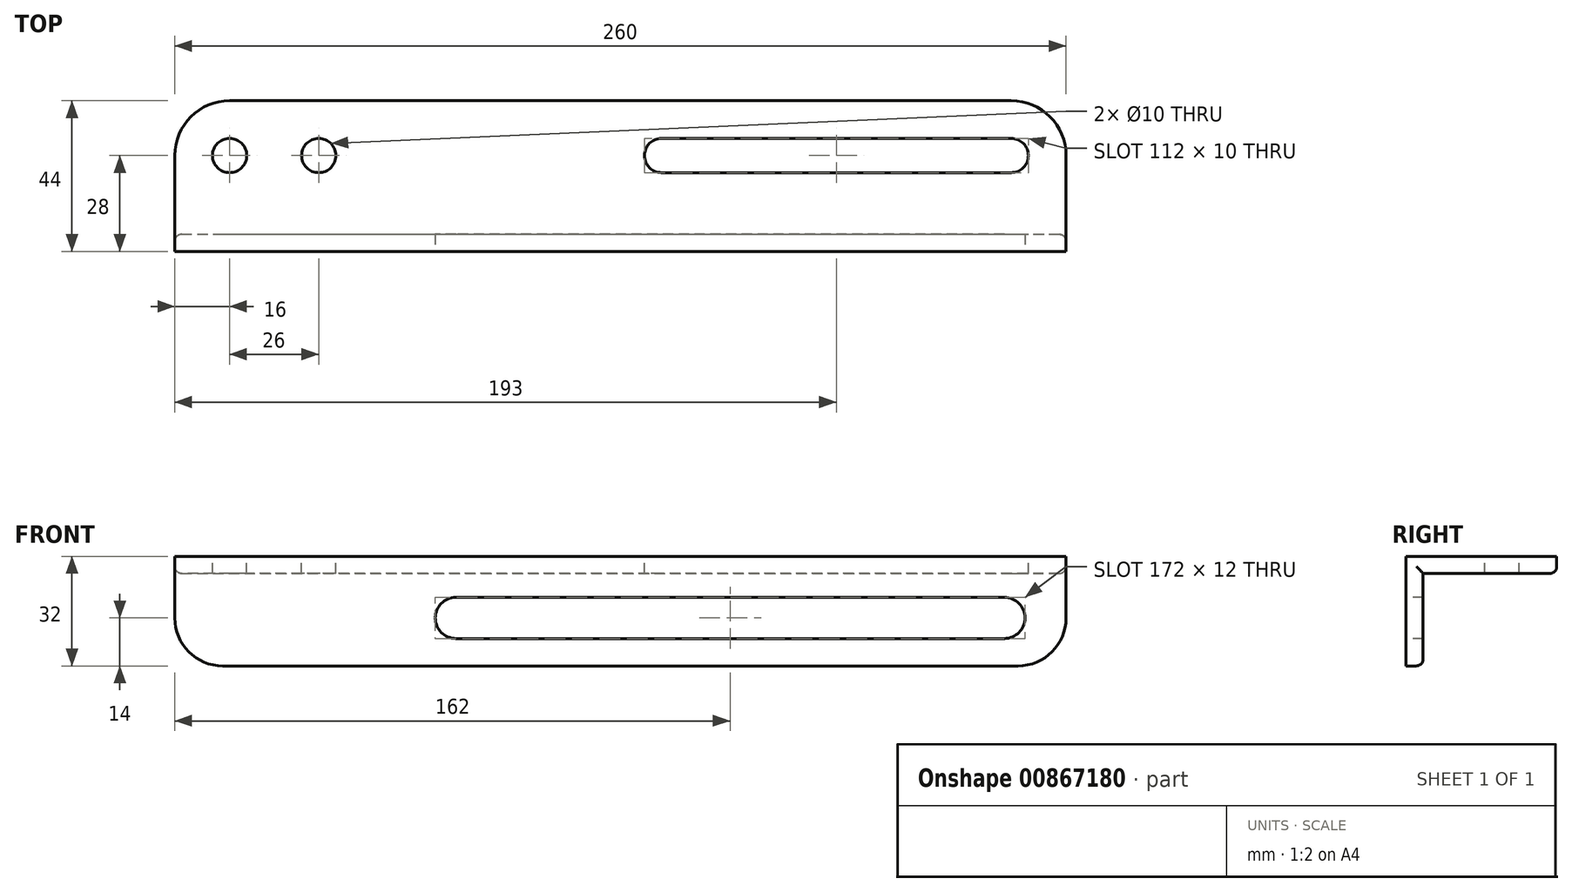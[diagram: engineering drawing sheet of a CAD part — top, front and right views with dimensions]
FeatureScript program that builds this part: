
annotation { "Feature Type Name" : "Feature", "Feature Type Description" : "" }
export const myFeature = defineFeature(function(context is Context, id is Id, definition is map)
    precondition{}
    {
        {
            var Q0;
            Q0=qCreatedBy(makeId("Top.planeOp"),FACE);
            var sketch = newSketch(context, id + "F0", { "sketchPlane" : qUnion([Q0])});
            skLineSegment(sketch, "E0", {"start": v(130, 0) * mm, "end": v(-130, 0) * mm});
            skLineSegment(sketch, "E1", {"start": v(130, 0) * mm, "end": v(130, 28) * mm});
            skLineSegment(sketch, "E2", {"start": v(114, 44) * mm, "end": v(-114, 44) * mm});
            skLineSegment(sketch, "E3", {"start": v(-130, 28) * mm, "end": v(-130, 0) * mm});
            skPoint(sketch, "E4.visualSharp", {"position": v(130, 44) * mm});
            skArc(sketch, "E4.filletArc", {"start": v(130, 28) * mm, "mid": v(125.31, 39.31) * mm, "end": v(114, 44) * mm});
            skPoint(sketch, "E5.visualSharp", {"position": v(-130, 44) * mm});
            skArc(sketch, "E5.filletArc", {"start": v(-114, 44) * mm, "mid": v(-125.31, 39.31) * mm, "end": v(-130, 28) * mm});
            skSolve(sketch);
        }
        {
            var Q0;
            Q0=makeQuery(id+"F0.imprint","IMPRINT",FACE,{"disambiguationData":[TD([[makeQuery(id+"F0.imprint","IMPRINT",EDGE,{"derivedFrom":sQuery(id+"F0.wireOp",EDGE,"E0")}),-1.0]])]});
            extrude(context, id + "F1", {"entities" : qUnion([Q0]), "oppositeDirection" : true, "depth" : 5 * mm, "offsetDistance" : 25 * mm});
        }
        {
            var Q0;
            Q0=makeQuery(id+"F1.opExtrude","CAP_FACE",FACE,{"disambiguationData":[OSD([sQuery(id+"F0.wireOp",EDGE,"E0"),sQuery(id+"F0.wireOp",EDGE,"E1"),sQuery(id+"F0.wireOp",EDGE,"E2"),sQuery(id+"F0.wireOp",EDGE,"E3"),sQuery(id+"F0.wireOp",EDGE,"E4.filletArc"),sQuery(id+"F0.wireOp",EDGE,"E5.filletArc")])],"isStart":true});
            var sketch = newSketch(context, id + "F2", { "sketchPlane" : qUnion([Q0])});
            skLineSegment(sketch, "E6", {"start": v(-149.8, 28) * mm, "end": v(123.32, 28) * mm, "construction": true});
            skLineSegment(sketch, "E7", {"start": v(-114, 41.85) * mm, "end": v(-114, -2.88) * mm, "construction": true});
            skLineSegment(sketch, "E8", {"start": v(-88, 42.48) * mm, "end": v(-88, -4.78) * mm, "construction": true});
            skCircle(sketch, "E9", {"center": v(-114, 28) * mm, "radius": 5 * mm});
            skCircle(sketch, "E10", {"center": v(-88, 28) * mm, "radius": 5 * mm});
            skLineSegment(sketch, "E11", {"start": v(12, 13.35) * mm, "end": v(12, 37.98) * mm, "construction": true});
            skLineSegment(sketch, "E12", {"start": v(114, 14.97) * mm, "end": v(114, 36.5) * mm, "construction": true});
            skLineSegment(sketch, "E13", {"start": v(114, 23) * mm, "end": v(12, 23) * mm});
            skLineSegment(sketch, "E14.MirrorCS", {"start": v(114, 33) * mm, "end": v(12, 33) * mm});
            skArc(sketch, "E15", {"start": v(12, 23) * mm, "mid": v(7, 28) * mm, "end": v(12, 33) * mm});
            skArc(sketch, "E16", {"start": v(114, 33) * mm, "mid": v(119, 28) * mm, "end": v(114, 23) * mm});
            skSolve(sketch);
        }
        {
            var Q0;
            Q0=makeQuery(id+"F2.imprint","IMPRINT",FACE,{"disambiguationData":[TD([[makeQuery(id+"F2.imprint","IMPRINT",EDGE,{"derivedFrom":sQuery(id+"F2.wireOp",EDGE,"E13")}),-1.0]])]});
            var Q1;
            Q1=makeQuery(id+"F2.imprint","IMPRINT",FACE,{"disambiguationData":[TD([[makeQuery(id+"F2.imprint","IMPRINT",EDGE,{"derivedFrom":sQuery(id+"F2.wireOp",EDGE,"E10")}),1.0]])]});
            var Q2;
            Q2=makeQuery(id+"F2.imprint","IMPRINT",FACE,{"disambiguationData":[TD([[makeQuery(id+"F2.imprint","IMPRINT",EDGE,{"derivedFrom":sQuery(id+"F2.wireOp",EDGE,"E9")}),1.0]])]});
            extrude(context, id + "F3", {"entities" : qUnion([Q0, Q1, Q2]), "operationType" : NewBodyOperationType.REMOVE, "oppositeDirection" : true, "depth" : 5 * mm, "offsetDistance" : 25 * mm});
        }
        {
            var Q0;
            Q0=makeQuery(id+"F1.opExtrude","CAP_FACE",FACE,{"disambiguationData":[OSD([sQuery(id+"F0.wireOp",EDGE,"E0"),sQuery(id+"F0.wireOp",EDGE,"E1"),sQuery(id+"F0.wireOp",EDGE,"E2"),sQuery(id+"F0.wireOp",EDGE,"E3"),sQuery(id+"F0.wireOp",EDGE,"E4.filletArc"),sQuery(id+"F0.wireOp",EDGE,"E5.filletArc")])],"isStart":false});
            var sketch = newSketch(context, id + "F4", { "sketchPlane" : qUnion([Q0])});
            skLineSegment(sketch, "E17", {"start": v(130, 0) * mm, "end": v(-130, 0) * mm});
            skLineSegment(sketch, "E18", {"start": v(-130, 0) * mm, "end": v(-130, -5) * mm});
            skLineSegment(sketch, "E19", {"start": v(-130, -5) * mm, "end": v(130, -5) * mm});
            skLineSegment(sketch, "E20", {"start": v(130, -5) * mm, "end": v(130, 0) * mm});
            skSolve(sketch);
        }
        {
            var Q0;
            Q0=makeQuery(id+"F4.imprint","IMPRINT",FACE,{"disambiguationData":[TD([[makeQuery(id+"F4.imprint","IMPRINT",EDGE,{"derivedFrom":sQuery(id+"F4.wireOp",EDGE,"E17")}),1.0]])]});
            extrude(context, id + "F5", {"entities" : qUnion([Q0]), "operationType" : NewBodyOperationType.ADD, "depth" : 27 * mm, "offsetDistance" : 25 * mm});
        }
        {
            var Q0;
            Q0=makeQuery(id+"F5.opExtrude","CAP_EDGE",EDGE,{"disambiguationData":[OSD([sQuery(id+"F4.wireOp",EDGE,"E20")])],"isStart":false});
            var Q1;
            Q1=makeQuery(id+"F5.opExtrude","CAP_EDGE",EDGE,{"disambiguationData":[OSD([sQuery(id+"F4.wireOp",EDGE,"E18")])],"isStart":false});
            fillet(context, id + "F6", {"entities" : qUnion([Q0, Q1]), "radius" : 14 * mm, "tangentPropagation" : true, "allowEdgeOverflow" : false});
        }
        {
            var Q0;
            Q0=makeQuery(id+"F5.boolean.opBoolean","MERGE",FACE,{"derivedFrom":[makeQuery(id+"F1.opExtrude","SWEPT_FACE",FACE,{"disambiguationData":[OSD([sQuery(id+"F0.wireOp",EDGE,"E0")])]}),makeQuery(id+"F5.opExtrude","SWEPT_FACE",FACE,{"disambiguationData":[OSD([sQuery(id+"F4.wireOp",EDGE,"E17")])]})]});
            var sketch = newSketch(context, id + "F7", { "sketchPlane" : qUnion([Q0])});
            skLineSegment(sketch, "E21", {"start": v(183.96, -18) * mm, "end": v(-135.14, -18) * mm, "construction": true});
            skLineSegment(sketch, "E22", {"start": v(112, 13.92) * mm, "end": v(112, -46.51) * mm, "construction": true});
            skLineSegment(sketch, "E23", {"start": v(-48, 7.81) * mm, "end": v(-48, -45.47) * mm, "construction": true});
            skLineSegment(sketch, "E24", {"start": v(112, -12) * mm, "end": v(-48, -12) * mm});
            skLineSegment(sketch, "E25.MirrorCS", {"start": v(112, -24) * mm, "end": v(-48, -24) * mm});
            skArc(sketch, "E26", {"start": v(-48, -24) * mm, "mid": v(-54, -18) * mm, "end": v(-48, -12) * mm});
            skArc(sketch, "E27", {"start": v(112, -12) * mm, "mid": v(118, -18) * mm, "end": v(112, -24) * mm});
            skSolve(sketch);
        }
        {
            var Q0;
            Q0 = qSketchRegion(id + "F7", true);
            extrude(context, id + "F8", {"entities" : qUnion([Q0]), "operationType" : NewBodyOperationType.REMOVE, "oppositeDirection" : true, "depth" : 5 * mm, "offsetDistance" : 25 * mm});
        }
        {
            var Q0;
            Q0=makeQuery(id+"F5.opExtrude","CAP_EDGE",EDGE,{"disambiguationData":[OSD([sQuery(id+"F4.wireOp",EDGE,"E19")])],"isStart":false});
            var Q1;
            Q1=makeQuery(id+"F1.opExtrude","CAP_EDGE",EDGE,{"disambiguationData":[OSD([sQuery(id+"F0.wireOp",EDGE,"E2")])],"isStart":false});
            var Q2;
            Q2=makeQuery(id+"F5.opExtrude","CAP_EDGE",EDGE,{"disambiguationData":[OSD([sQuery(id+"F4.wireOp",EDGE,"E19")])],"isStart":true});
            fillet(context, id + "F9", {"entities" : qUnion([Q0, Q1, Q2]), "radius" : 2 * mm, "tangentPropagation" : true, "allowEdgeOverflow" : false});
        }
    });
